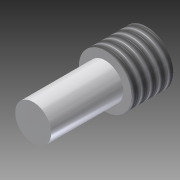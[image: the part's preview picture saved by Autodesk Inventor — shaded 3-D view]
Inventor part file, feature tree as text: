
AUTODESK INVENTOR PART (.ipt)
format: ipt  version: 2012 (Build 160160000, 160)  size: 91,136 bytes
history: native  units: in
note: dims shown in document units (in); Inventor stores cm internally (conversion verified against a paired STEP export)
features: extrude x2, sketch x1, thread x1
ambient origin geometry x8: Origin, YZ Plane, XZ Plane, XY Plane, X Axis, Y Axis, Z Axis, Center Point
bodies: Solid1 (feature_tree)
feature tree (4):
  sketch  "Sketch1"  dims[d0=0.366in d1=0.25in d2=0.288in d3=0.0in d4=0.5in d5=0.0in d6=1.0in d7=0.0in]
  extrude  "Extrusion1"  Depth=0.25in
  extrude  "Extrusion2"  Depth=0.288in TaperAngle=0.0deg
  thread  "Thread1"  [1 undecoded]
note: 1 required parameter value undecoded (feature->parameter linkage not recoverable at this tier; creation-order binding heuristic only, values carry confidence <= 0.55)
